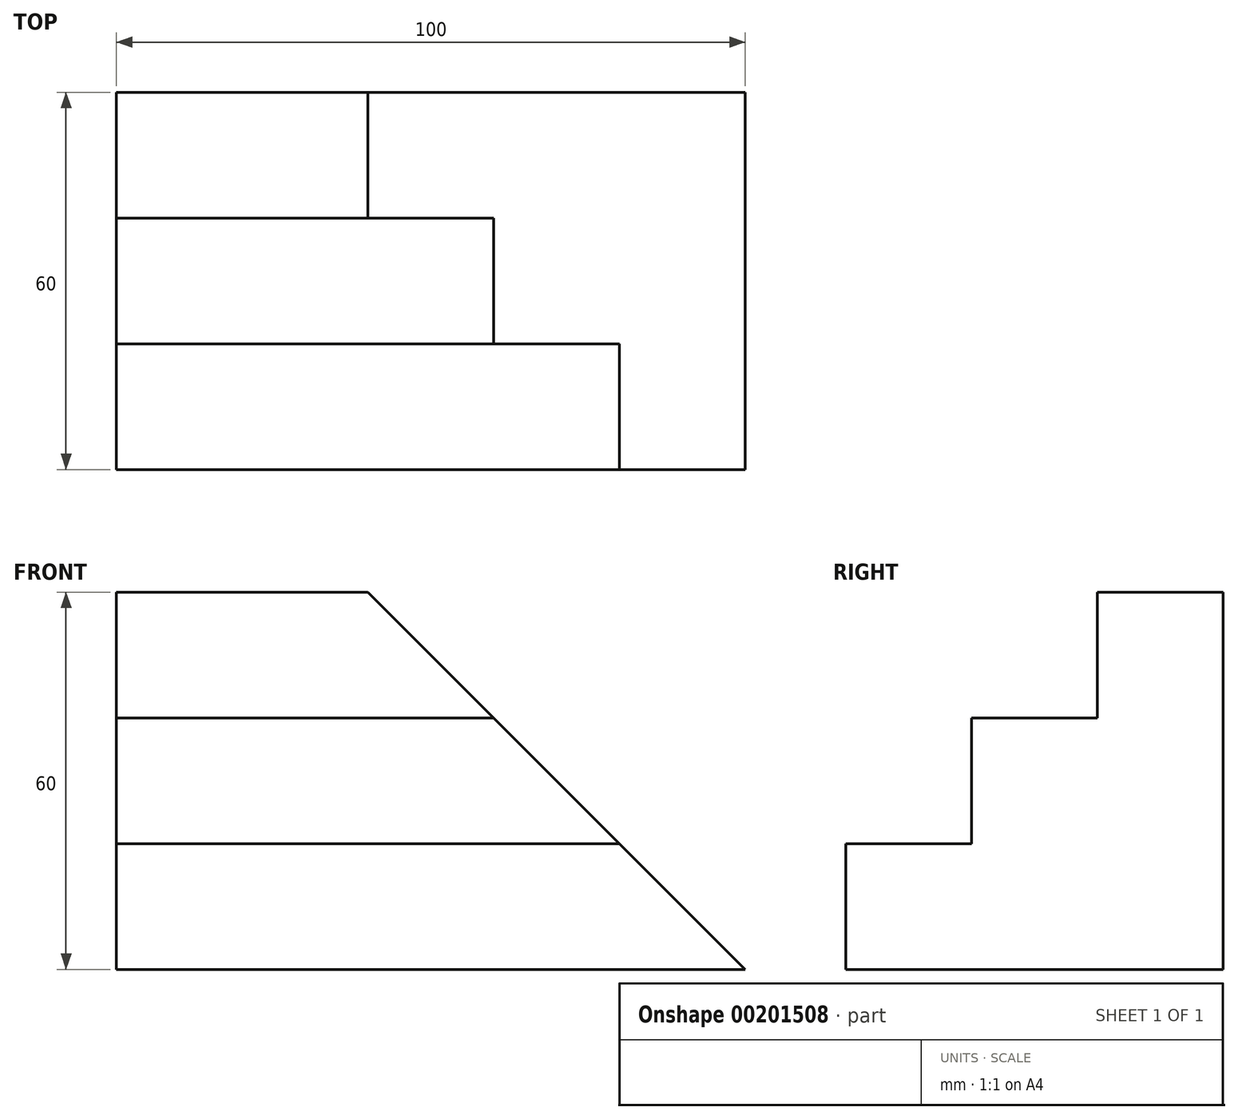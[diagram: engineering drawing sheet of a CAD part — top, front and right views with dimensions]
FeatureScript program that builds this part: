
annotation { "Feature Type Name" : "Feature", "Feature Type Description" : "" }
export const myFeature = defineFeature(function(context is Context, id is Id, definition is map)
    precondition{}
    {
        {
            var Q0;
            Q0=qCreatedBy(makeId("Right.planeOp"),FACE);
            var sketch = newSketch(context, id + "F0", { "sketchPlane" : qUnion([Q0])});
            skLineSegment(sketch, "E0", {"start": v(0, 0) * mm, "end": v(0, 60) * mm});
            skLineSegment(sketch, "E1", {"start": v(0, 60) * mm, "end": v(-20, 60) * mm});
            skLineSegment(sketch, "E2", {"start": v(-20, 60) * mm, "end": v(-20, 40) * mm});
            skLineSegment(sketch, "E3", {"start": v(-20, 40) * mm, "end": v(-40, 40) * mm});
            skLineSegment(sketch, "E4", {"start": v(-40, 40) * mm, "end": v(-40, 20) * mm});
            skLineSegment(sketch, "E5", {"start": v(-40, 20) * mm, "end": v(-60, 20) * mm});
            skLineSegment(sketch, "E6", {"start": v(-60, 20) * mm, "end": v(-60, 0) * mm});
            skLineSegment(sketch, "E7", {"start": v(-60, 0) * mm, "end": v(0, 0) * mm});
            skSolve(sketch);
        }
        {
            var Q0;
            Q0=qSketchRegion(id+"F0",true);
            extrude(context, id + "F1", {"entities" : qUnion([Q0]), "depth" : 110 * mm});
        }
        {
            var Q0;
            Q0=makeQuery(id+"F1.opExtrude","CAP_EDGE",EDGE,{"disambiguationData":[OSD([sQuery(id+"F0.wireOp",EDGE,"E1")])],"isStart":false});
            chamfer(context, id + "F2", {"entities" : qUnion([Q0]), "width" : (110 - 40) * mm, "tangentPropagation" : true});
        }
    });
